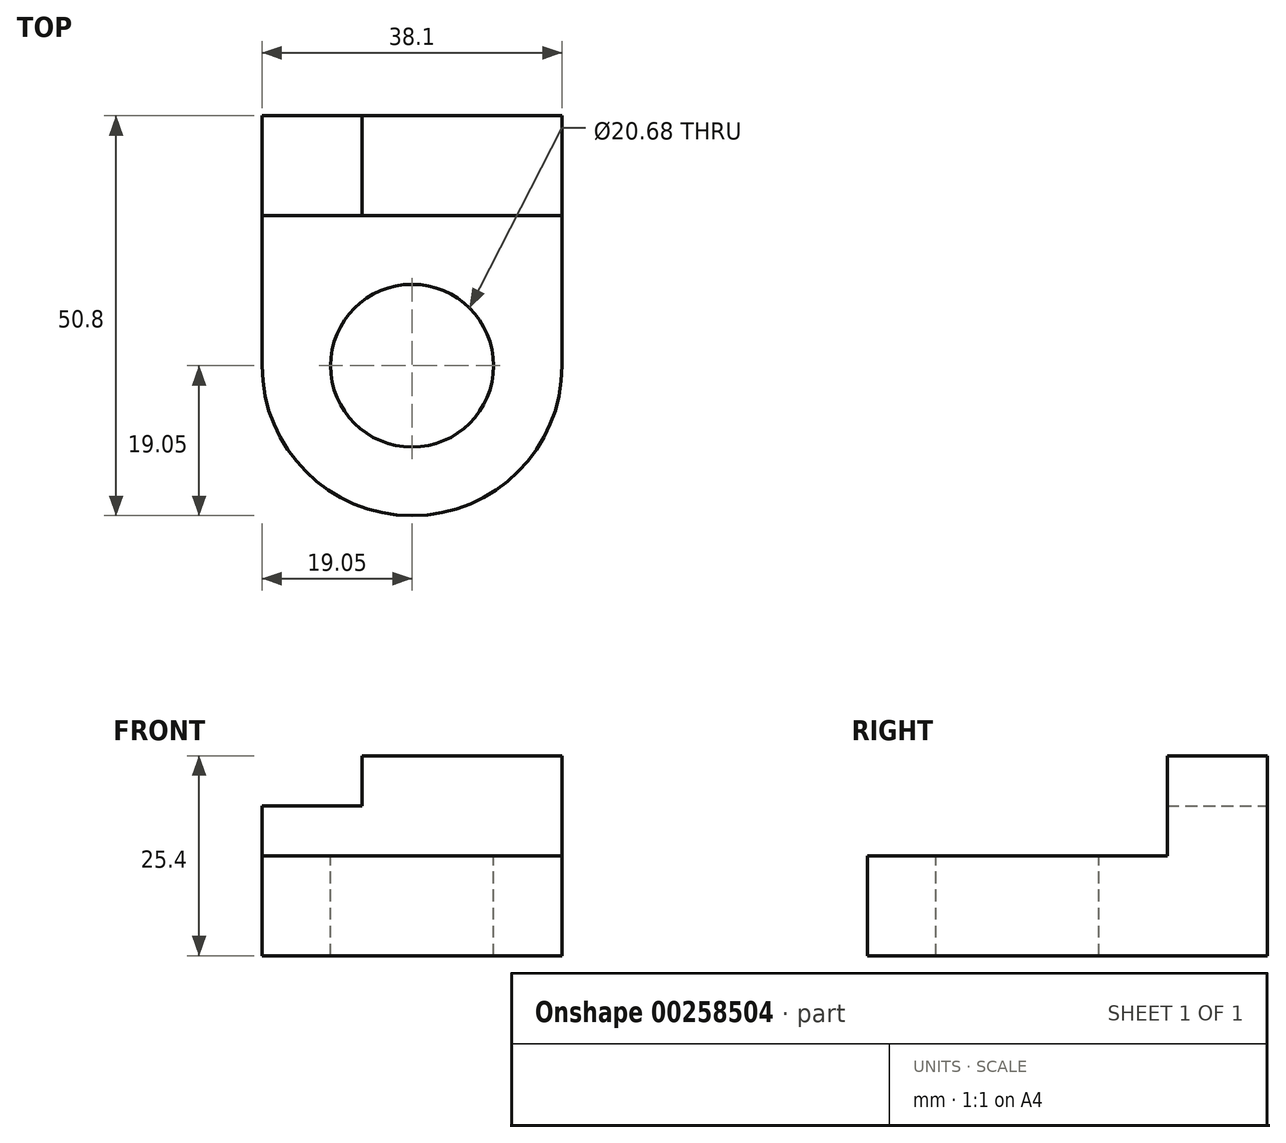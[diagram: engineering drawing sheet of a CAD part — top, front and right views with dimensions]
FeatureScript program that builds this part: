
annotation { "Feature Type Name" : "Feature", "Feature Type Description" : "" }
export const myFeature = defineFeature(function(context is Context, id is Id, definition is map)
    precondition{}
    {
        {
            var Q0;
            Q0=qCreatedBy(makeId("Top.planeOp"),FACE);
            var sketch = newSketch(context, id + "F0", { "sketchPlane" : qUnion([Q0])});
            skLineSegment(sketch, "E0.bottom", {"start": v(19.05, 25.4) * mm, "end": v(-19.05, 25.4) * mm});
            skLineSegment(sketch, "E0.top", {"start": v(19.05, -25.4) * mm, "end": v(-19.05, -25.4) * mm});
            skLineSegment(sketch, "E0.left", {"start": v(19.05, 25.4) * mm, "end": v(19.05, -25.4) * mm});
            skLineSegment(sketch, "E0.right", {"start": v(-19.05, 25.4) * mm, "end": v(-19.05, -25.4) * mm});
            skPoint(sketch, "E0.middle", {"position": v(0, 0) * mm});
            skSolve(sketch);
        }
        {
            var Q0;
            Q0=makeQuery(id+"F0.imprint","IMPRINT",FACE,{"disambiguationData":[TD([[makeQuery(id+"F0.imprint","IMPRINT",EDGE,{"derivedFrom":sQuery(id+"F0.wireOp",EDGE,"E0.bottom")}),1.0]])]});
            var sketch = newSketch(context, id + "F1", { "sketchPlane" : qUnion([Q0])});
            skLineSegment(sketch, "E1.bottom", {"start": v(19.05, 25.4) * mm, "end": v(-6.35, 25.4) * mm});
            skLineSegment(sketch, "E1.top", {"start": v(19.05, 12.7) * mm, "end": v(-6.35, 12.7) * mm});
            skLineSegment(sketch, "E1.left", {"start": v(19.05, 25.4) * mm, "end": v(19.05, 12.7) * mm});
            skLineSegment(sketch, "E1.right", {"start": v(-6.35, 25.4) * mm, "end": v(-6.35, 12.7) * mm});
            skLineSegment(sketch, "E2.bottom", {"start": v(-6.35, 25.4) * mm, "end": v(-19.05, 25.4) * mm});
            skLineSegment(sketch, "E2.top", {"start": v(-6.35, 12.7) * mm, "end": v(-19.05, 12.7) * mm});
            skLineSegment(sketch, "E2.right", {"start": v(-19.05, 25.4) * mm, "end": v(-19.05, 12.7) * mm});
            skSolve(sketch);
        }
        {
            var Q0;
            Q0=makeQuery(id+"F1.imprint","IMPRINT",FACE,{"disambiguationData":[TD([[makeQuery(id+"F1.imprint","IMPRINT",EDGE,{"derivedFrom":sQuery(id+"F1.wireOp",EDGE,"E1.bottom")}),1.0]])]});
            extrude(context, id + "F2", {"entities" : qUnion([Q0]), "depth" : 25.4 * mm});
        }
        {
            var Q0;
            Q0=makeQuery(id+"F0.imprint","IMPRINT",FACE,{"disambiguationData":[TD([[makeQuery(id+"F0.imprint","IMPRINT",EDGE,{"derivedFrom":sQuery(id+"F0.wireOp",EDGE,"E0.bottom")}),1.0]])]});
            extrude(context, id + "F3", {"entities" : qUnion([Q0]), "operationType" : NewBodyOperationType.ADD, "depth" : 12.7 * mm});
        }
        {
            var Q0;
            Q0=makeQuery(id+"F3.opExtrude","CAP_FACE",FACE,{"disambiguationData":[OSD([sQuery(id+"F0.wireOp",EDGE,"E0.bottom"),sQuery(id+"F0.wireOp",EDGE,"E0.top"),sQuery(id+"F0.wireOp",EDGE,"E0.left"),sQuery(id+"F0.wireOp",EDGE,"E0.right")])],"isStart":false});
            var sketch = newSketch(context, id + "F4", { "sketchPlane" : qUnion([Q0])});
            skCircle(sketch, "E3", {"center": v(0, -6.35) * mm, "radius": 10.34 * mm});
            skSolve(sketch);
        }
        {
            var Q0;
            Q0=makeQuery(id+"F4.imprint","IMPRINT",FACE,{"disambiguationData":[TD([[makeQuery(id+"F4.imprint","IMPRINT",EDGE,{"derivedFrom":sQuery(id+"F4.wireOp",EDGE,"E3")}),1.0]])]});
            extrude(context, id + "F5", {"entities" : qUnion([Q0]), "operationType" : NewBodyOperationType.REMOVE, "endBound" : BoundingType.THROUGH_ALL, "oppositeDirection" : true, "depth" : 25.4 * mm});
        }
        {
            var Q0;
            Q0=makeQuery(id+"F3.opExtrude","SWEPT_EDGE",EDGE,{"disambiguationData":[OSD([sQuery(id+"F0.wireOp",EDGE,"E0.top"),sQuery(id+"F0.wireOp",EDGE,"E0.right")])]});
            var Q1;
            Q1=makeQuery(id+"F3.opExtrude","SWEPT_EDGE",EDGE,{"disambiguationData":[OSD([sQuery(id+"F0.wireOp",EDGE,"E0.top"),sQuery(id+"F0.wireOp",EDGE,"E0.left")])]});
            fillet(context, id + "F6", {"entities" : qUnion([Q0, Q1]), "radius" : 19.05 * mm, "tangentPropagation" : true, "allowEdgeOverflow" : false});
        }
        {
            var Q0;
            Q0=makeQuery(id+"F2.opExtrude","SWEPT_FACE",FACE,{"disambiguationData":[OSD([sQuery(id+"F1.wireOp",EDGE,"E1.right")])]});
            var sketch = newSketch(context, id + "F7", { "sketchPlane" : qUnion([Q0])});
            skLineSegment(sketch, "E4.bottom", {"start": v(-12.7, 12.7) * mm, "end": v(-25.4, 12.7) * mm});
            skLineSegment(sketch, "E4.top", {"start": v(-12.7, 19.05) * mm, "end": v(-25.4, 19.05) * mm});
            skLineSegment(sketch, "E4.left", {"start": v(-12.7, 12.7) * mm, "end": v(-12.7, 19.05) * mm});
            skLineSegment(sketch, "E4.right", {"start": v(-25.4, 12.7) * mm, "end": v(-25.4, 19.05) * mm});
            skSolve(sketch);
        }
        {
            var Q0;
            Q0=makeQuery(id+"F7.imprint","IMPRINT",FACE,{"disambiguationData":[TD([[makeQuery(id+"F7.imprint","IMPRINT",EDGE,{"derivedFrom":sQuery(id+"F7.wireOp",EDGE,"E4.bottom")}),1.0]])]});
            extrude(context, id + "F8", {"entities" : qUnion([Q0]), "operationType" : NewBodyOperationType.ADD, "depth" : 12.7 * mm});
        }
    });
